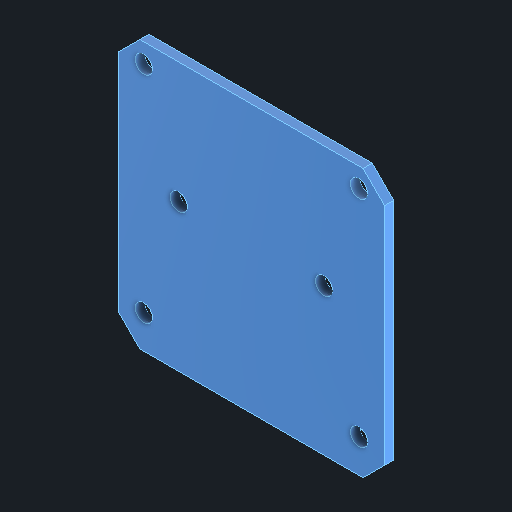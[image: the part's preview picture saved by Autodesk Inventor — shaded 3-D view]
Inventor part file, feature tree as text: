
AUTODESK INVENTOR PART (.ipt)
format: ipt  version: 2024 (Build 280153000, 153)  size: 104,448 bytes
history: native  units: mm
features: other x1, chamfer x1
ambient origin geometry x8: Origin, YZ Plane, XZ Plane, XY Plane, X Axis, Y Axis, Z Axis, Center Point
bodies: Body1 (feature_tree)
feature tree (2):
  other  "Твердое тело1"
  chamfer  "Chamfer1"  [1 undecoded]
note: 1 required parameter value undecoded (feature->parameter linkage not recoverable at this tier; creation-order binding heuristic only, values carry confidence <= 0.55)
